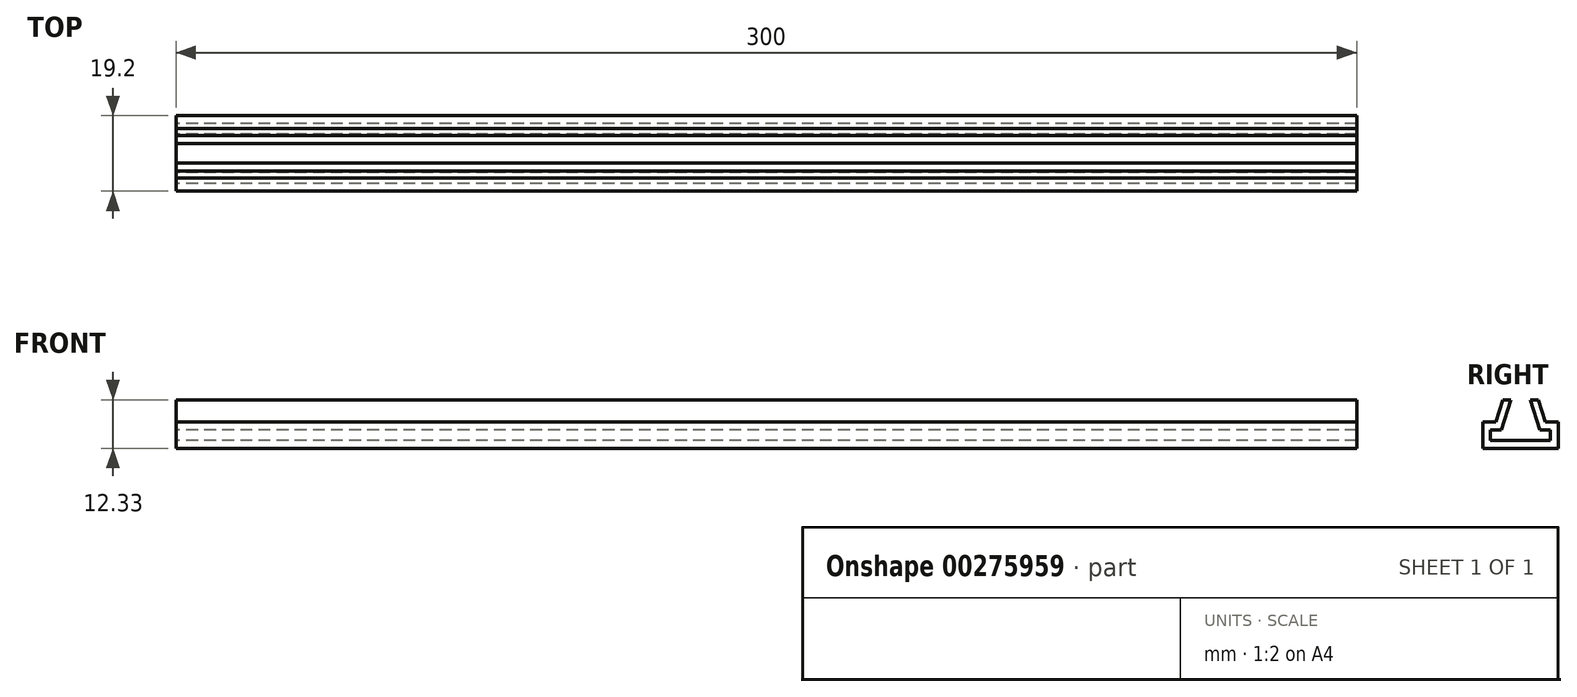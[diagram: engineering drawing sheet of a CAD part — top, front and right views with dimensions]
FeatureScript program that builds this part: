
annotation { "Feature Type Name" : "Feature", "Feature Type Description" : "" }
export const myFeature = defineFeature(function(context is Context, id is Id, definition is map)
    precondition{}
    {
        {
            var Q0;
            Q0=qCreatedBy(makeId("Right.planeOp"),FACE);
            var sketch = newSketch(context, id + "F0", { "sketchPlane" : qUnion([Q0])});
            skLineSegment(sketch, "E0", {"start": v(30.09, 16.43) * mm, "end": v(27.69, 8.8) * mm});
            skLineSegment(sketch, "E1", {"start": v(27.69, 8.8) * mm, "end": v(24.99, 8.8) * mm});
            skLineSegment(sketch, "E2", {"start": v(24.99, 8.8) * mm, "end": v(24.99, 6.1) * mm});
            skLineSegment(sketch, "E3", {"start": v(24.99, 6.1) * mm, "end": v(40.19, 6.1) * mm});
            skLineSegment(sketch, "E4", {"start": v(40.19, 6.1) * mm, "end": v(40.19, 8.8) * mm});
            skLineSegment(sketch, "E5", {"start": v(40.19, 8.8) * mm, "end": v(37.49, 8.8) * mm});
            skLineSegment(sketch, "E6", {"start": v(37.49, 8.8) * mm, "end": v(35.09, 16.43) * mm});
            skLineSegment(sketch, "E7", {"start": v(35.09, 16.43) * mm, "end": v(37.09, 16.43) * mm});
            skLineSegment(sketch, "E8", {"start": v(37.09, 16.43) * mm, "end": v(38.86, 10.8) * mm});
            skLineSegment(sketch, "E9", {"start": v(38.86, 10.8) * mm, "end": v(42.19, 10.8) * mm});
            skLineSegment(sketch, "E10", {"start": v(42.19, 10.8) * mm, "end": v(42.19, 4.1) * mm});
            skLineSegment(sketch, "E11", {"start": v(42.19, 4.1) * mm, "end": v(22.99, 4.1) * mm});
            skLineSegment(sketch, "E12", {"start": v(22.99, 4.1) * mm, "end": v(22.99, 10.8) * mm});
            skLineSegment(sketch, "E13", {"start": v(22.99, 10.8) * mm, "end": v(26.32, 10.8) * mm});
            skLineSegment(sketch, "E14", {"start": v(26.32, 10.8) * mm, "end": v(28.09, 16.43) * mm});
            skLineSegment(sketch, "E15", {"start": v(28.09, 16.43) * mm, "end": v(30.09, 16.43) * mm});
            skSolve(sketch);
        }
        {
            var Q0;
            Q0=makeQuery(id+"F0.imprint","IMPRINT",FACE,{"disambiguationData":[TD([[makeQuery(id+"F0.imprint","IMPRINT",EDGE,{"derivedFrom":sQuery(id+"F0.wireOp",EDGE,"E0")}),-1.0]])]});
            extrude(context, id + "F1", {"entities" : qUnion([Q0]), "depth" : 300 * mm});
        }
    });
